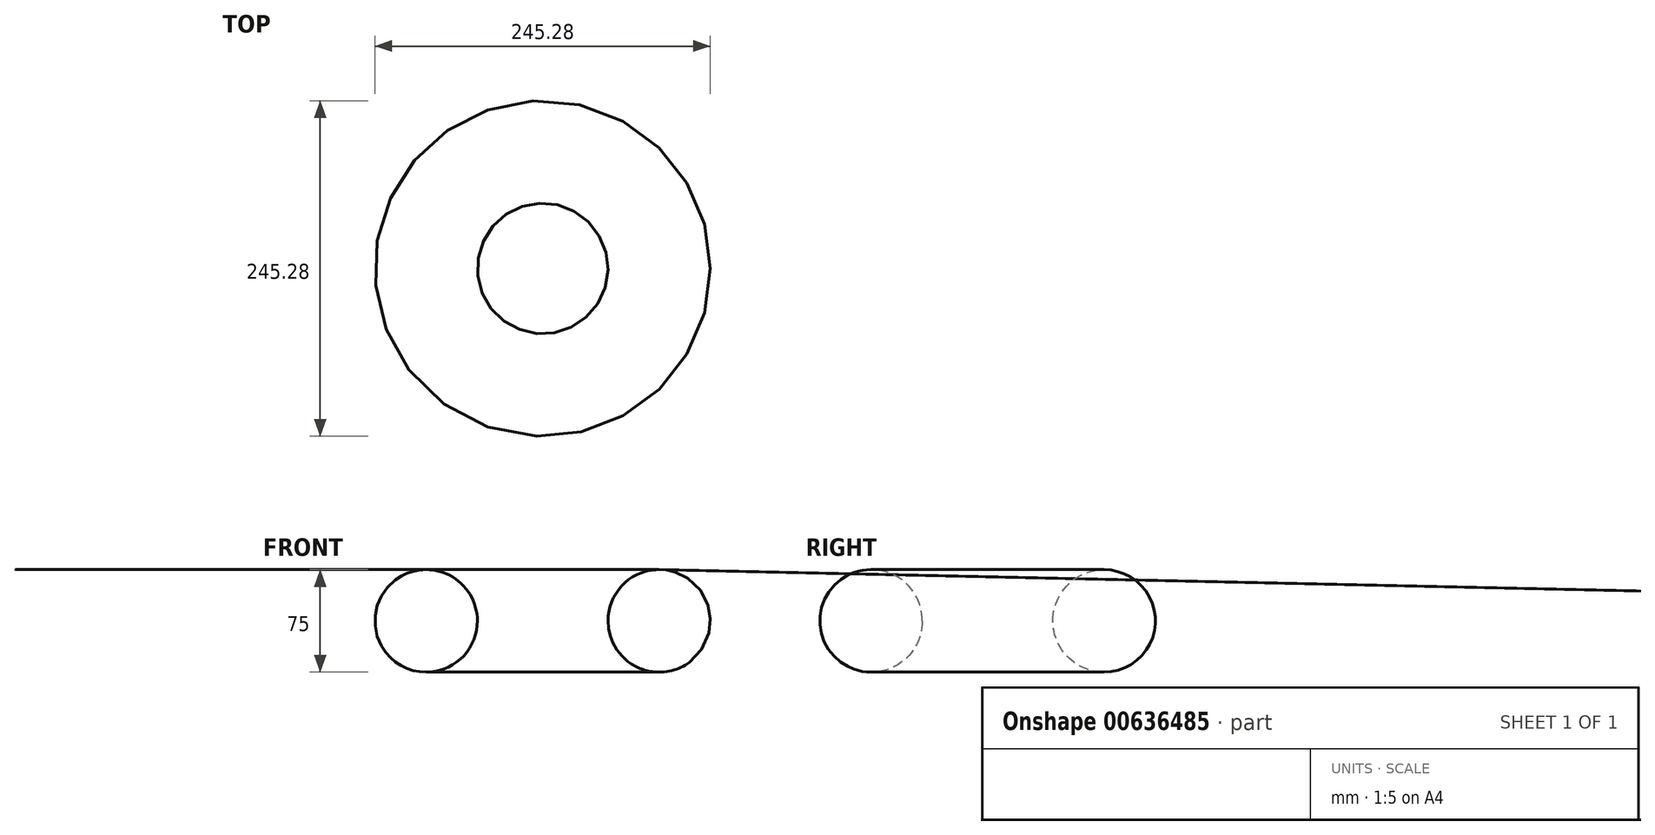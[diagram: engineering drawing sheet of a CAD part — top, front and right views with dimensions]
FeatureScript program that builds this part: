
annotation { "Feature Type Name" : "Feature", "Feature Type Description" : "" }
export const myFeature = defineFeature(function(context is Context, id is Id, definition is map)
    precondition{}
    {
        {
            var Q0;
            Q0=qCreatedBy(makeId("Right.planeOp"),FACE);
            var sketch = newSketch(context, id + "F0", { "sketchPlane" : qUnion([Q0])});
            skCircle(sketch, "E0", {"center": v(0, 0) * mm, "radius": 37.5 * mm});
            skSolve(sketch);
        }
        {
            var Q0;
            Q0=qCreatedBy(makeId("Top.planeOp"),FACE);
            var sketch = newSketch(context, id + "F1", { "sketchPlane" : qUnion([Q0])});
            skCircle(sketch, "E1", {"center": v(4.32, 85.06) * mm, "radius": 85.17 * mm});
            skPoint(sketch, "E1.first.point", {"position": v(0, 0) * mm});
            skPoint(sketch, "E1.second.point", {"position": v(0, 170.12) * mm});
            skPoint(sketch, "E1.third.point", {"position": v(88.6, 97.36) * mm});
            skSolve(sketch);
        }
        {
            var Q0;
            Q0=makeQuery(id+"F0.imprint","IMPRINT",FACE,{"disambiguationData":[TD([[makeQuery(id+"F0.imprint","IMPRINT",EDGE,{"derivedFrom":sQuery(id+"F0.wireOp",EDGE,"E0")}),1.0]])]});
            var Q1;
            Q1=sQuery(id+"F0.wireOp",EDGE,"E0");
            var Q2;
            Q2=sQuery(id+"F1.wireOp",EDGE,"E1");
            revolve(context, id + "F2", {"bodyType" : ToolBodyType.SURFACE, "entities" : qUnion([Q0]), "surfaceEntities" : qUnion([Q1]), "axis" : qUnion([Q2]), "revolveType" : RevolveType.FULL});
        }
    });
